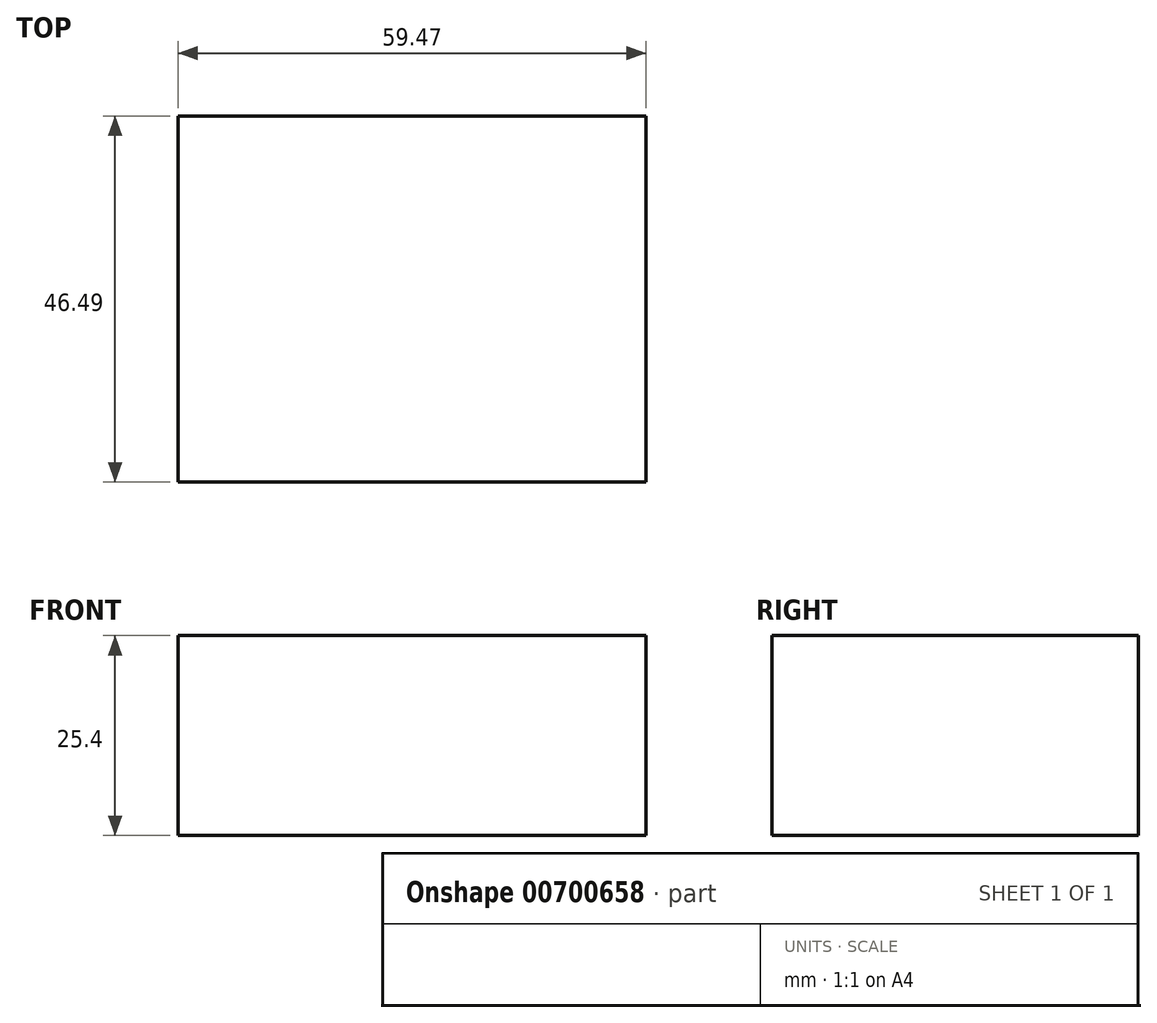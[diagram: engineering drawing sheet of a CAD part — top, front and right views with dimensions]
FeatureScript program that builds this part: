
annotation { "Feature Type Name" : "Feature", "Feature Type Description" : "" }
export const myFeature = defineFeature(function(context is Context, id is Id, definition is map)
    precondition{}
    {
        {
            var Q0;
            Q0=qCreatedBy(makeId("Top.planeOp"),FACE);
            var sketch = newSketch(context, id + "F0", { "sketchPlane" : qUnion([Q0])});
            skLineSegment(sketch, "E0.bottom", {"start": v(0, 0) * mm, "end": v(-59.47, 0) * mm});
            skLineSegment(sketch, "E0.top", {"start": v(0, 46.5) * mm, "end": v(-59.47, 46.5) * mm});
            skLineSegment(sketch, "E0.left", {"start": v(0, 0) * mm, "end": v(0, 46.5) * mm});
            skLineSegment(sketch, "E0.right", {"start": v(-59.47, 0) * mm, "end": v(-59.47, 46.5) * mm});
            skSolve(sketch);
        }
        {
            var Q0;
            Q0 = qSketchRegion(id + "F0", true);
            extrude(context, id + "F1", {"entities" : qUnion([Q0]), "depth" : 25.4 * mm, "offsetDistance" : 25.4 * mm});
        }
    });
